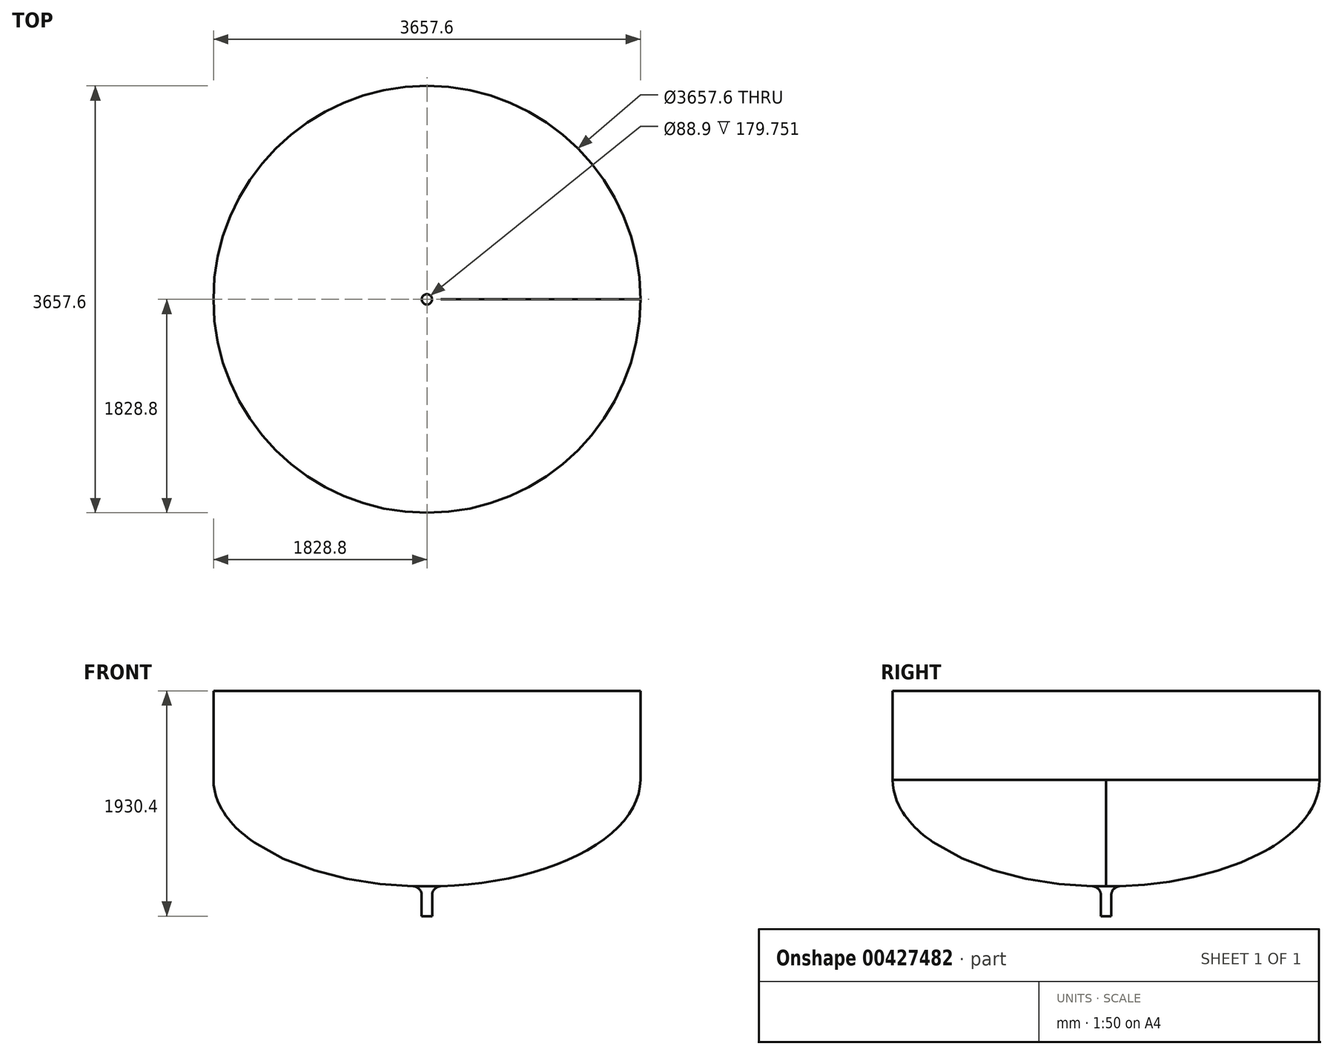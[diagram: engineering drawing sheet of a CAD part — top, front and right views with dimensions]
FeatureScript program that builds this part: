
annotation { "Feature Type Name" : "Feature", "Feature Type Description" : "" }
export const myFeature = defineFeature(function(context is Context, id is Id, definition is map)
    precondition{}
    {
        {
            var Q0;
            Q0=qCreatedBy(makeId("Front.planeOp"),FACE);
            var sketch = newSketch(context, id + "F0", { "sketchPlane" : qUnion([Q0])});
            skEllipticalArc(sketch, "E0", {});
            skLineSegment(sketch, "E1", {"start": v(0, 0) * mm, "end": v(1828.8, 0) * mm, "construction": true});
            skPoint(sketch, "E2", {"position": v(0, -914.4) * mm});
            skLineSegment(sketch, "E3", {"start": v(0, -914.4) * mm, "end": v(0, 762) * mm, "construction": true});
            skLineSegment(sketch, "E4", {"start": v(0, 762) * mm, "end": v(1828.8, 762) * mm, "construction": true});
            skPoint(sketch, "E5.end.orphan", {"position": v(0, 762) * mm});
            skPoint(sketch, "E6.orphan", {"position": v(-1828.8, 0) * mm});
            skLineSegment(sketch, "E7", {"start": v(0, -1168.4) * mm, "end": v(44.45, -1168.4) * mm});
            skLineSegment(sketch, "E8", {"start": v(44.45, -1168.4) * mm, "end": v(44.45, -988.65) * mm});
            skArc(sketch, "E9.filletArc", {"start": v(118.18, -912.49) * mm, "mid": v(65.9, -935.65) * mm, "end": v(44.45, -988.65) * mm});
            skLineSegment(sketch, "E10.trimOffspring", {"start": v(1828.8, 0) * mm, "end": v(1828.8, 762) * mm});
            const initialGuessF0  = {"E0": [0, 0, 1, 0, 1.8288, 0.9144, 4.7770578258246665, 0]};
            skSetInitialGuess(sketch, initialGuessF0);
            skSolve(sketch);
        }
        {
            var Q0;
            Q0 = qSketchRegion(id + "F0", true);
            var Q1;
            Q1 = qConstructionFilter(qBodyType(qCreatedBy(id + "F0" ,EDGE), BodyType.WIRE), ConstructionObject.NO);
            var Q2;
            Q2=sQuery(id+"F0.wireOp",EDGE,"E3");
            revolve(context, id + "F1", {"bodyType" : ToolBodyType.SURFACE, "entities" : qUnion([Q0]), "surfaceEntities" : qUnion([Q1]), "axis" : qUnion([Q2]), "revolveType" : RevolveType.FULL});
        }
    });
